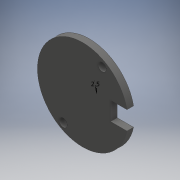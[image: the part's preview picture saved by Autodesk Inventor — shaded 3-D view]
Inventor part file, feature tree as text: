
AUTODESK INVENTOR PART (.ipt)
format: ipt  version: 2017 (Build 210142000, 142)  size: 168,448 bytes
history: native  units: mm
features: sketch x7, extrude x4, plane x1, revolve x1
ambient origin geometry x8: Origin, YZ Plane, XZ Plane, XY Plane, X Axis, Y Axis, Z Axis, Center Point
bodies: Solid1 (feature_tree)
feature tree (13):
  extrude  "Extrusion1"  Depth=2.0mm
  extrude  "Extrusion2"  Depth=1.6mm TaperAngle=0.0deg
  sketch  "Sketch3"  dims[d11=2.5mm d12=1.6mm d13=0.0mm]
  plane  "Work Plane1"
  revolve  "Revolution1"  [1 undecoded]
  extrude  "Extrusion3"  TaperAngle=90.0deg  [1 undecoded]
  sketch  "Sketch6"  dims[d20=60.0deg]
  extrude  "Extrusion4"  Depth=1.6mm TaperAngle=0.0deg
  sketch  "Sketch1"  dims[d1=19.0mm d7=2.0mm]
  sketch  "Sketch2"  dims[d8=2.0mm d9=1.6mm d10=0.0mm]
  sketch  "Sketch4"  dims[d14=2.5mm d16=90.0deg]
  sketch  "Sketch5"  dims[d17=90.0deg d18=1.6mm d19=0.0mm]
  sketch  "Sketch7"  dims[d21=0.2mm d22=0.0mm]
note: 2 required parameter values undecoded (feature->parameter linkage not recoverable at this tier; creation-order binding heuristic only, values carry confidence <= 0.55)